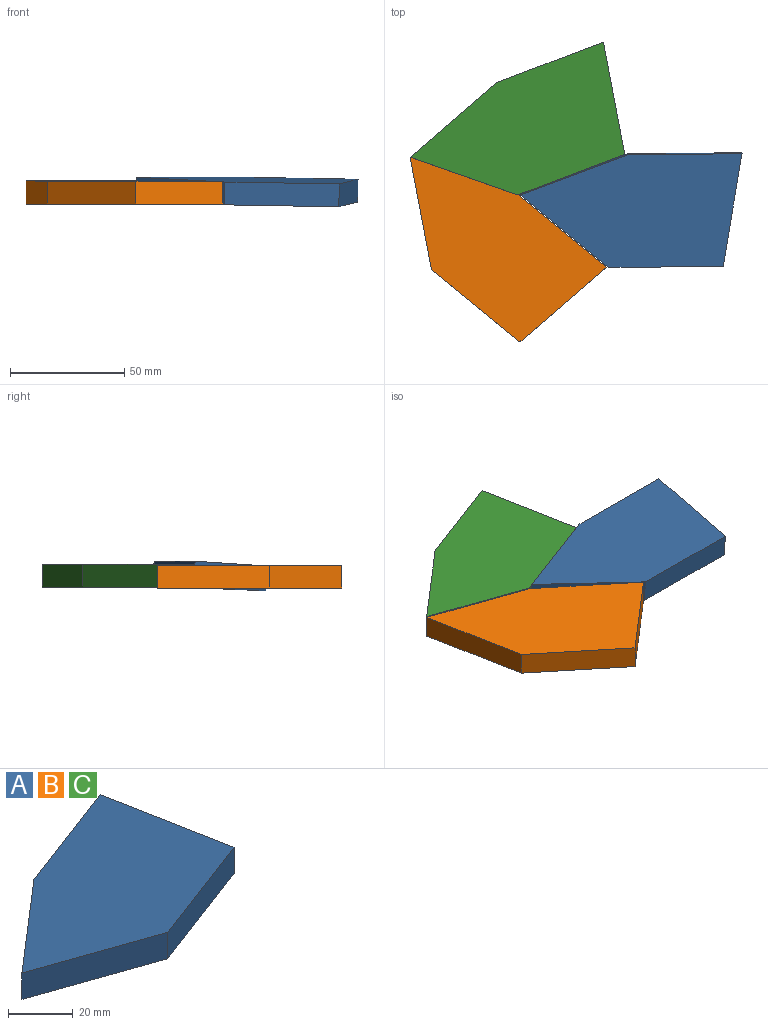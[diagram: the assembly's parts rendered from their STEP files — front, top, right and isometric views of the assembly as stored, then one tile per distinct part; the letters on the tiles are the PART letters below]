
ASSEMBLY  parts=3 mates=1
PART A: 7 faces, bbox 94x66.8x10 mm
  f0: plane 37.87x32.64mm, normal (-0.65,0.76,0), area 500mm2, adj f1,f4,f5,f6
  f1: plane 47.21x16.48mm, normal (-0.33,-0.94,0), area 500mm2, adj f0,f2,f5,f6
  f2: plane 46.75x17.72mm, normal (0.35,-0.94,0), area 500mm2, adj f1,f3,f5,f6
  f3: plane 49.12x10mm, normal (0.98,0.19,0), area 500mm2, adj f2,f4,f5,f6
  f4: plane 46.75x17.72mm, normal (-0.35,0.94,0), area 500mm2, adj f0,f3,f5,f6
  f5: plane 93.96x66.84mm, normal (0,0,1), area 3544.6mm2, adj f0,f1,f2,f3,f4
  f6: plane 93.96x66.84mm, normal (0,0,-1), area 3544.6mm2, adj f0,f1,f2,f3,f4
PART B: same geometry as A
PART C: same geometry as A
PLACE A rot(axis=(0.12,0.07,-0.99),20.4deg) t=(20.27,-19.79,-0.26)mm
PLACE B rot(axis=(0,0,-1),60deg) t=(-27.93,-3.71,-1.99)mm
PLACE C t=(-27.99,-3.69,-1.56)mm fixed
MATE planar C.f1 <-> B.f0  axis (-0.33,-0.94,0) through (-4.39,-11.93,3.44)mm
